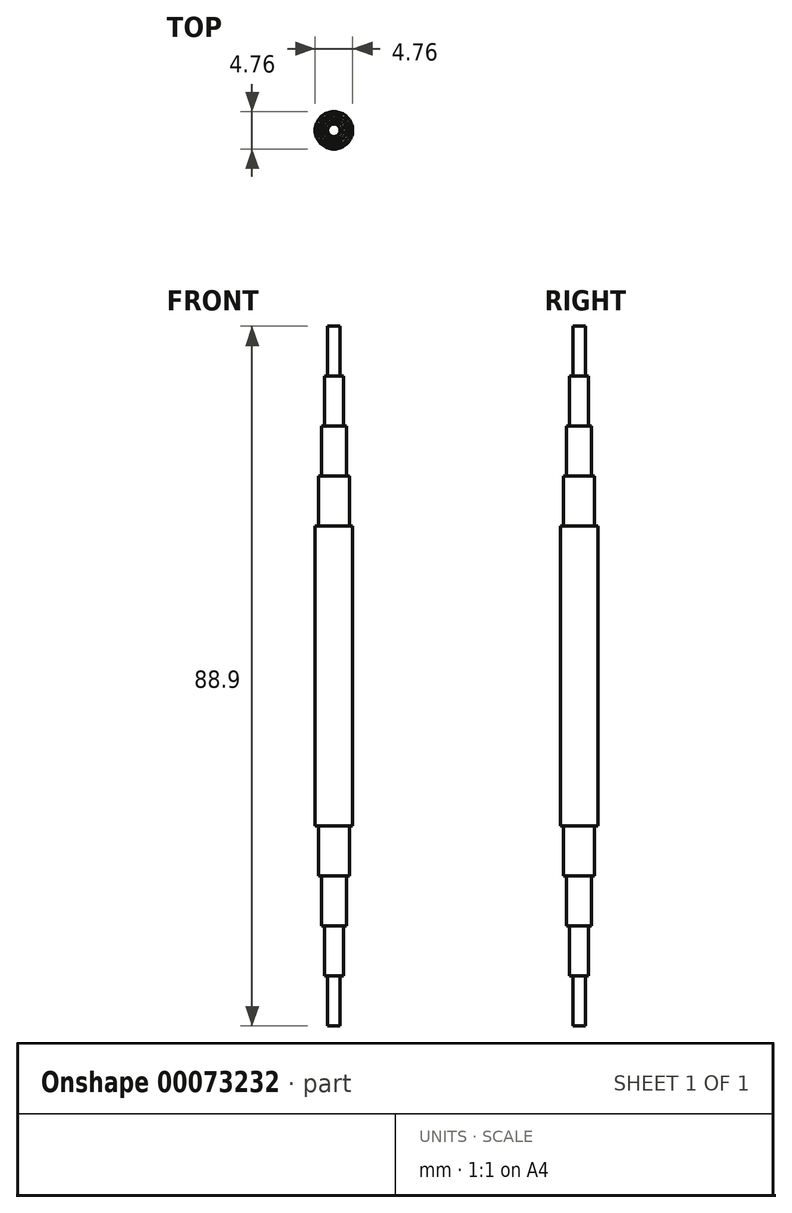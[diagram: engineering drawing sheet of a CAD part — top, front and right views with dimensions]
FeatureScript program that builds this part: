
annotation { "Feature Type Name" : "Feature", "Feature Type Description" : "" }
export const myFeature = defineFeature(function(context is Context, id is Id, definition is map)
    precondition{}
    {
        {
            var Q0;
            Q0=qCreatedBy(makeId("Front.planeOp"),FACE);
            var sketch = newSketch(context, id + "F0", { "sketchPlane" : qUnion([Q0])});
            skLineSegment(sketch, "E0", {"start": v(0, 61.63) * mm, "end": v(0, -46.56) * mm, "construction": true});
            skLineSegment(sketch, "E1", {"start": v(-41.89, 0) * mm, "end": v(45.2, 0) * mm, "construction": true});
            skLineSegment(sketch, "E2", {"start": v(0, 19.05) * mm, "end": v(2.38, 19.05) * mm});
            skLineSegment(sketch, "E3", {"start": v(2.38, 19.05) * mm, "end": v(2.38, 0) * mm});
            skLineSegment(sketch, "E4", {"start": v(2.38, -19.05) * mm, "end": v(0, -19.05) * mm});
            skLineSegment(sketch, "E5", {"start": v(1.98, 19.05) * mm, "end": v(1.98, 25.4) * mm});
            skLineSegment(sketch, "E6", {"start": v(1.98, 25.4) * mm, "end": v(0, 25.4) * mm});
            skLineSegment(sketch, "E7", {"start": v(0, 25.4) * mm, "end": v(0, 19.05) * mm});
            skLineSegment(sketch, "E8", {"start": v(0, 0) * mm, "end": v(0, 19.05) * mm});
            skLineSegment(sketch, "E9", {"start": v(2.38, 0) * mm, "end": v(0, 0) * mm});
            skLineSegment(sketch, "E10", {"start": v(0, 25.4) * mm, "end": v(0, 31.75) * mm});
            skLineSegment(sketch, "E11", {"start": v(0, 31.75) * mm, "end": v(1.59, 31.75) * mm});
            skLineSegment(sketch, "E12", {"start": v(1.59, 31.75) * mm, "end": v(1.59, 25.4) * mm});
            skLineSegment(sketch, "E13", {"start": v(0, 38.1) * mm, "end": v(0, 31.75) * mm});
            skLineSegment(sketch, "E14", {"start": v(0, 44.45) * mm, "end": v(0, 38.1) * mm});
            skLineSegment(sketch, "E15", {"start": v(0, 38.1) * mm, "end": v(1.2, 38.1) * mm});
            skLineSegment(sketch, "E16", {"start": v(1.2, 38.1) * mm, "end": v(1.2, 31.75) * mm});
            skLineSegment(sketch, "E17", {"start": v(0, 44.45) * mm, "end": v(0.8, 44.45) * mm});
            skLineSegment(sketch, "E18", {"start": v(0.8, 44.45) * mm, "end": v(0.8, 38.1) * mm});
            skSolve(sketch);
        }
        {
            var Q0;
            {var subQ1=sQuery(id+"F0.wireOp",EDGE,"E3");Q0=makeQuery(id+"F0.imprint","IMPRINT",FACE,{"disambiguationData":[TD([[makeQuery(id+"F0.imprint","IMPRINT",EDGE,{"derivedFrom":subQ1}),-1.0]])]});}
            var Q1;
            {var subQ3=sQuery(id+"F0.wireOp",EDGE,"E5");Q1=makeQuery(id+"F0.imprint","IMPRINT",FACE,{"disambiguationData":[TD([[makeQuery(id+"F0.imprint","IMPRINT",EDGE,{"derivedFrom":subQ3}),1.0]])]});}
            var Q2;
            {var subQ3=sQuery(id+"F0.wireOp",EDGE,"E10");Q2=makeQuery(id+"F0.imprint","IMPRINT",FACE,{"disambiguationData":[TD([[makeQuery(id+"F0.imprint","IMPRINT",EDGE,{"derivedFrom":subQ3}),-1.0]])]});}
            var Q3;
            {var subQ3=sQuery(id+"F0.wireOp",EDGE,"E13");Q3=makeQuery(id+"F0.imprint","IMPRINT",FACE,{"disambiguationData":[TD([[makeQuery(id+"F0.imprint","IMPRINT",EDGE,{"derivedFrom":subQ3}),1.0]])]});}
            var Q4;
            {var subQ0=sQuery(id+"F0.wireOp",EDGE,"E14");Q4=makeQuery(id+"F0.imprint","IMPRINT",FACE,{"disambiguationData":[TD([[makeQuery(id+"F0.imprint","IMPRINT",EDGE,{"derivedFrom":subQ0}),1.0]])]});}
            var Q5;
            Q5=sQuery(id+"F0.wireOp",EDGE,"E8");
            revolve(context, id + "F1", {"entities" : qUnion([Q0, Q1, Q2, Q3, Q4]), "axis" : qUnion([Q5]), "revolveType" : RevolveType.FULL});
        }
        {
            var Q0;
            Q0=makeQuery(id+"F1.opRevolve","SWEPT_BODY",BODY,{"disambiguationData":[OSD([sQuery(id+"F0.wireOp",EDGE,"E2"),sQuery(id+"F0.wireOp",EDGE,"E3"),sQuery(id+"F0.wireOp",EDGE,"E5"),sQuery(id+"F0.wireOp",EDGE,"E6"),sQuery(id+"F0.wireOp",EDGE,"E7"),sQuery(id+"F0.wireOp",EDGE,"E8"),sQuery(id+"F0.wireOp",EDGE,"E9"),sQuery(id+"F0.wireOp",EDGE,"E10"),sQuery(id+"F0.wireOp",EDGE,"E11"),sQuery(id+"F0.wireOp",EDGE,"E12"),sQuery(id+"F0.wireOp",EDGE,"E13"),sQuery(id+"F0.wireOp",EDGE,"E14"),sQuery(id+"F0.wireOp",EDGE,"E15"),sQuery(id+"F0.wireOp",EDGE,"E16"),sQuery(id+"F0.wireOp",EDGE,"E17"),sQuery(id+"F0.wireOp",EDGE,"E18")])]});
            var Q1;
            Q1=qCreatedBy(makeId("Top.planeOp"),FACE);
            mirror(context, id + "F2", {"operationType" : NewBodyOperationType.ADD, "entities" : qUnion([Q0]), "mirrorPlane" : qUnion([Q1])});
        }
    });
